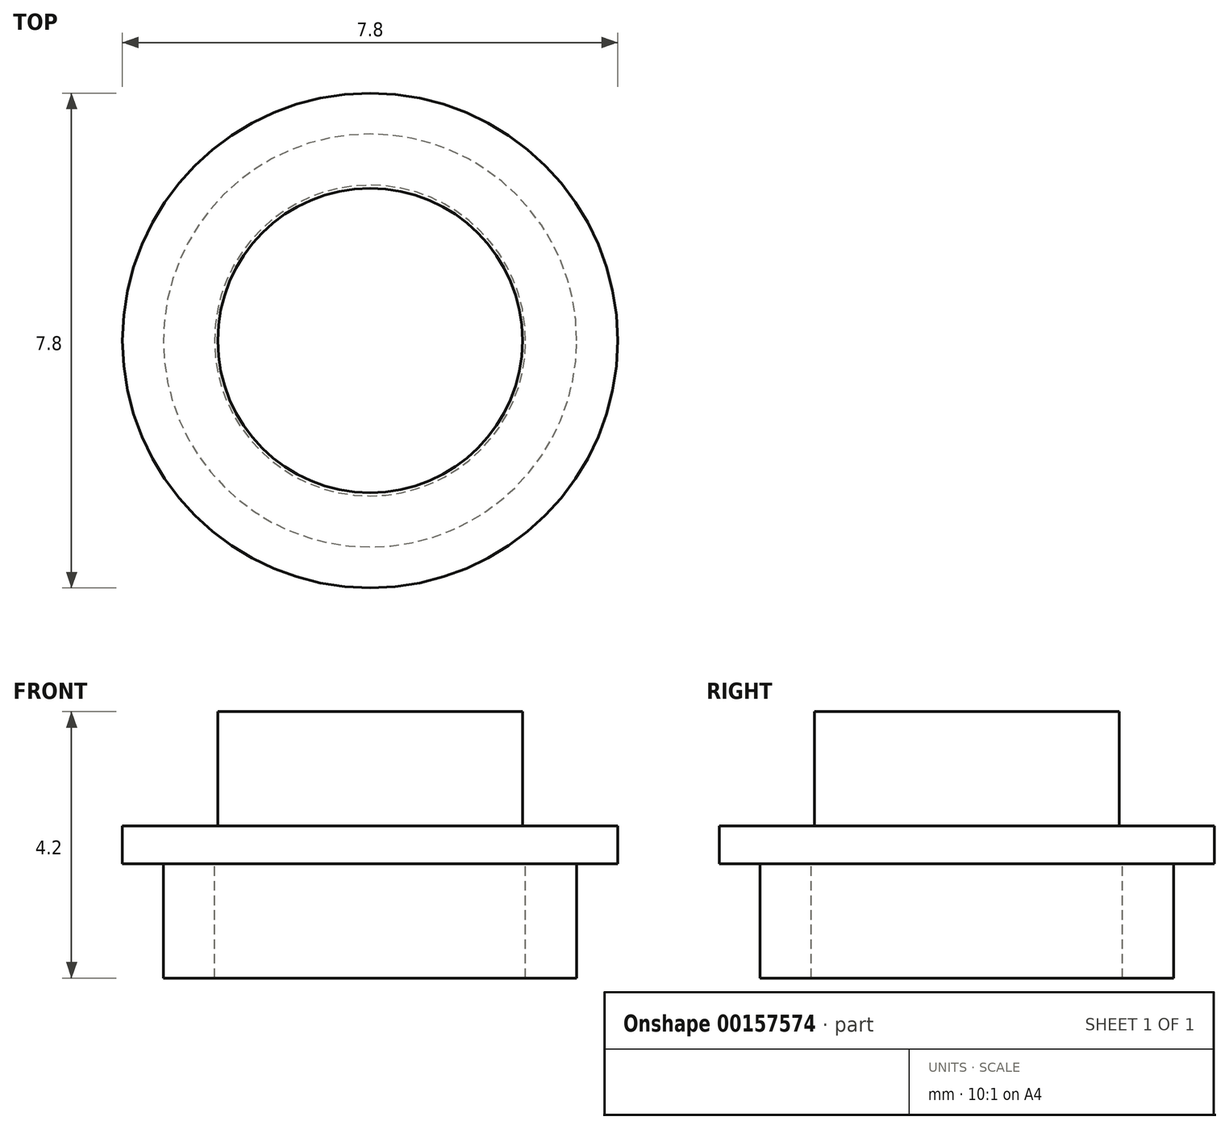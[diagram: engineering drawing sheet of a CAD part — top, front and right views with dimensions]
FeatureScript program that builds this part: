
annotation { "Feature Type Name" : "Feature", "Feature Type Description" : "" }
export const myFeature = defineFeature(function(context is Context, id is Id, definition is map)
    precondition{}
    {
        {
            var Q0;
            Q0=qCreatedBy(makeId("Front.planeOp"),FACE);
            var sketch = newSketch(context, id + "F0", { "sketchPlane" : qUnion([Q0])});
            skLineSegment(sketch, "E0", {"start": v(0, 50) * mm, "end": v(0, -50) * mm, "construction": true});
            skLineSegment(sketch, "E1", {"start": v(0, 0) * mm, "end": v(2.4, 0) * mm});
            skLineSegment(sketch, "E2", {"start": v(2.4, 0) * mm, "end": v(2.4, -1.8) * mm});
            skLineSegment(sketch, "E3", {"start": v(2.4, -1.8) * mm, "end": v(3.9, -1.8) * mm});
            skLineSegment(sketch, "E4", {"start": v(3.9, -1.8) * mm, "end": v(3.9, -2.4) * mm});
            skLineSegment(sketch, "E5", {"start": v(3.9, -2.4) * mm, "end": v(3.25, -2.4) * mm});
            skLineSegment(sketch, "E6", {"start": v(3.25, -2.4) * mm, "end": v(3.25, -4.2) * mm});
            skLineSegment(sketch, "E7", {"start": v(3.25, -4.2) * mm, "end": v(2.45, -4.2) * mm});
            skLineSegment(sketch, "E8", {"start": v(2.45, -4.2) * mm, "end": v(2.45, -2.4) * mm});
            skLineSegment(sketch, "E9", {"start": v(2.45, -2.4) * mm, "end": v(0, -2.4) * mm});
            skLineSegment(sketch, "E10", {"start": v(0, -2.4) * mm, "end": v(0, 0) * mm});
            skSolve(sketch);
        }
        {
            var Q0;
            Q0 = qSketchRegion(id + "F0", true);
            var Q1;
            Q1=sQuery(id+"F0.wireOp",EDGE,"E0");
            revolve(context, id + "F1", {"entities" : qUnion([Q0]), "axis" : qUnion([Q1]), "revolveType" : RevolveType.FULL});
        }
    });
